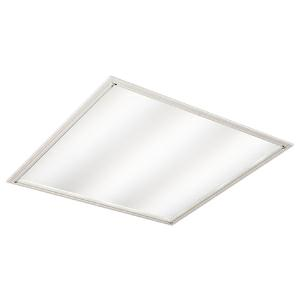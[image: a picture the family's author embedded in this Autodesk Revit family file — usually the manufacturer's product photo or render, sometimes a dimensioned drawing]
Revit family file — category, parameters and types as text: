
# Revit family: 3f_filippi_-_l_320_lgs_3f_filippi_-_22711_-_l_324x10w-940_led_ep_lgs_596x596
name_source: partatom
category: Lighting Fixtures
units: mm (PartAtom-declared; Revit-internal decimal feet)

## family parameters
Cut with Voids When Loaded = No
Host = Face
Light Source = No
Part Type = Normal
Room Calculation Point = No
Round Connector Dimension = Use Diameter
Shared = No

## types (1)
- 3F Filippi - L 320 LGS (1 x LED, 3327 lm, 46 W, 4000 K)
    Apparent Load = 46 VA
    Approval mark = ENEC
    CIE Flux Codes = 62 88 97 100 100
    Color Rendering = 90
    Color Temperature = 4000 K
    Control Gear = Electronic ballast
    Default Elevation = 1800 mm
    Description = ILLUMINOTECHNICAL
Luminous efficiency 100% (DLOR 100%, ULOR 0%).
Initial luminous flux of the luminaire 3327 lm.
Emergency luminaire luminous flux BLF 8.6%.
Direct symmetric distribution.
Installation Interdistance Transv.D = 1.16 x hu - Long.D = 1.16 x hu.
Average luminance <3000 cd/m² for radial angles >65°.
Tabular UGR (CIE 117 - 4H-8H; S=0.25H; 70/50/20): RUG 17.9 - 17.9.
Beam angle: 85° - 84°.
Luminous efficacy 72 lm/W.
Lifetime (L93/B10): 30000 h. (tq+25°C)
Lifetime (L90/B10): 50000 h. (tq+25°C)
Lifetime (L85/B10): 80000 h. (tq+25°C)
Lifetime (L80/B10): 100000 h. (tq+25°C)
Sudden decreased luminous flux after 50000 hours: 0% (C0).
Photobiological safety in compliance with IEC/TR 62778: RG0 risk exempt, (IEC 62471).
In compliance with IEC/EN 62722-2-1 - IEC/EN 62717 standards.

SOURCE
4 linear LED modules 10W/940.
Energy efficiency class (UE 2019/2020 - UE 2019/2015): E.
CIE 13.3 Colour rendering index: CRI >90 (R9 >50%).
IES TM-30 Fidelity Index: Rf = 92 Rg = 101.
CCT nominal colour temperature 4000 K.
Colour initial tolerance (MacAdam): SDCM 2.

MECHANICAL
Housing in hot-galvanised steel, painted in white polyester.
Micro-prismatic flat diffuser in transparent methacrylate (PMMA), multilenticular exterior, anti-glare, locked to the white painted aluminium perimetral frame, sealing gasket, hinged opening.
Anti-glare opal polycarbonate filter for brightness uniformity.
Luminaire with limited surface temperature. - D - (EN 60598-2-24)
Dimensions: 596x596 mm, height 80 mm. Weight 5.6 kg.
IP54 protection degree for exposed part, IP20 for recessed part.
Mechanical strength to impacts IK06 (1 joule).
Glow-wire test resistance 650°C.

ELECTRICAL
Halogen Free electronic wiring 230V-50/60Hz, power factor 0.90, THD <25%, constant output current, SELV, class I, 1 driver.
Power of the luminaire 46 W.
CE - IEC 60598-1 - EN 60598-1.
EP maintained emergency wiring on board, 1h duration, 24h recharge; compliant with EN 60598-2-22, excluding high risk areas.
SAFE FLICKER: PstLM=<1 and SVM=<0.4 (IEC TR 61547-1 and IEC TR 63158), to ensure a more comfortable and safe light.
Ambient temperature from +5°C to +25°C.
Temperature class T6 max 85°C.
Relative humidity UR: <85%.

INSTALLATION
Lay-in recessed fitting.
On request: pull-up recessed fitting with brackets.
False ceiling carving: 580x580 mm.
All accessories dedicated to this product are available on the Catalog and on our website www.3F-Filippi.com.

APPLICATIONS
Environments: sterilized, aseptic.
In environments with VDU's, managerial offices and staterooms, environments involving accurate visual tasks where a diffused and soft light for an optimum visual comfort and the source total shielding are required.

WARNING
Luminaire designed for disposal/recycling at end-of-life.
Replaceable (LED only) light source by a professional. Replaceable control gear by a professional.
    Height = 0 mm  [stored 0 ft]
    Lamp = 1 x LED
    Lamp Light Flux = 3327 lm
    Lamp Power = 46 W
    Lamp count = 1
    Length = 596 mm
    Lifetime = 50000 h
    Luminous efficacy = 72 lm/W
    Manufacturer = 3F Filippi
    ModVariant = No
    Model = 3F Filippi - 22711 - L 324x10W-940 LED EP LGS 596x596
    Mounting Place = Ceiling
    Mounting Type = Recessed
    Number of Poles = 1
    OnlyDefault = Yes
    Power Factor = 1
    Product Name = 3F Filippi - L 320 LGS
    Product group = recessed luminaire
    ProductGroupID = 4
    Protection Class = Protection class I
    Protection Degree = IP 20
    RLX_Detail_Level = 1
    RLX_Emergency_Light_Flux = 0 lm
    RLX_Emergency_Type = 0
    RLX_Emergency_Type_DB = No
    RlxData = <blob elided: 33841 chars, md5=c99f06cb>
    Socket = socket
    Standby Power = 0 W
    System Light Flux = 3327 lm
    System Power = 46 W
    Type Comments = Product without accessories
    Type Image = 3ffilippi_l_320_led_lgs.jpg
    URL = http://relux.com
    VarID = ---
    Voltage = 0 V
    Weight = 0.00 kg
    Width = 596 mm

note: [stored X ft] marks values corroborated as IEEE doubles in the binary element streams (Revit-internal decimal feet)

## geometry (parser evidence)
native form markers: Blend x4, Sweep x8
no freeform markers — native parametric forms only
